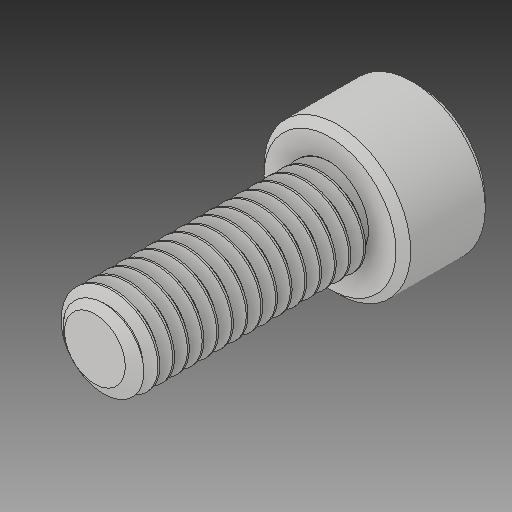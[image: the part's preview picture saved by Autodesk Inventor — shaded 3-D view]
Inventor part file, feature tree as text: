
AUTODESK INVENTOR PART (.ipt)
format: ipt  version: 2018 (Build 220112000, 112)  size: 809,472 bytes
history: native  units: in
note: dims shown in document units (in); Inventor stores cm internally (conversion verified against a paired STEP export)
features: chamfer x1
ambient origin geometry x8: Origin, YZ Plane, XZ Plane, XY Plane, X Axis, Y Axis, Z Axis, Center Point
bodies: Solid1 (feature_tree)
feature tree (1):
  chamfer  "Chamfer1"  [1 undecoded]
note: 1 required parameter value undecoded (feature->parameter linkage not recoverable at this tier; creation-order binding heuristic only, values carry confidence <= 0.55)
